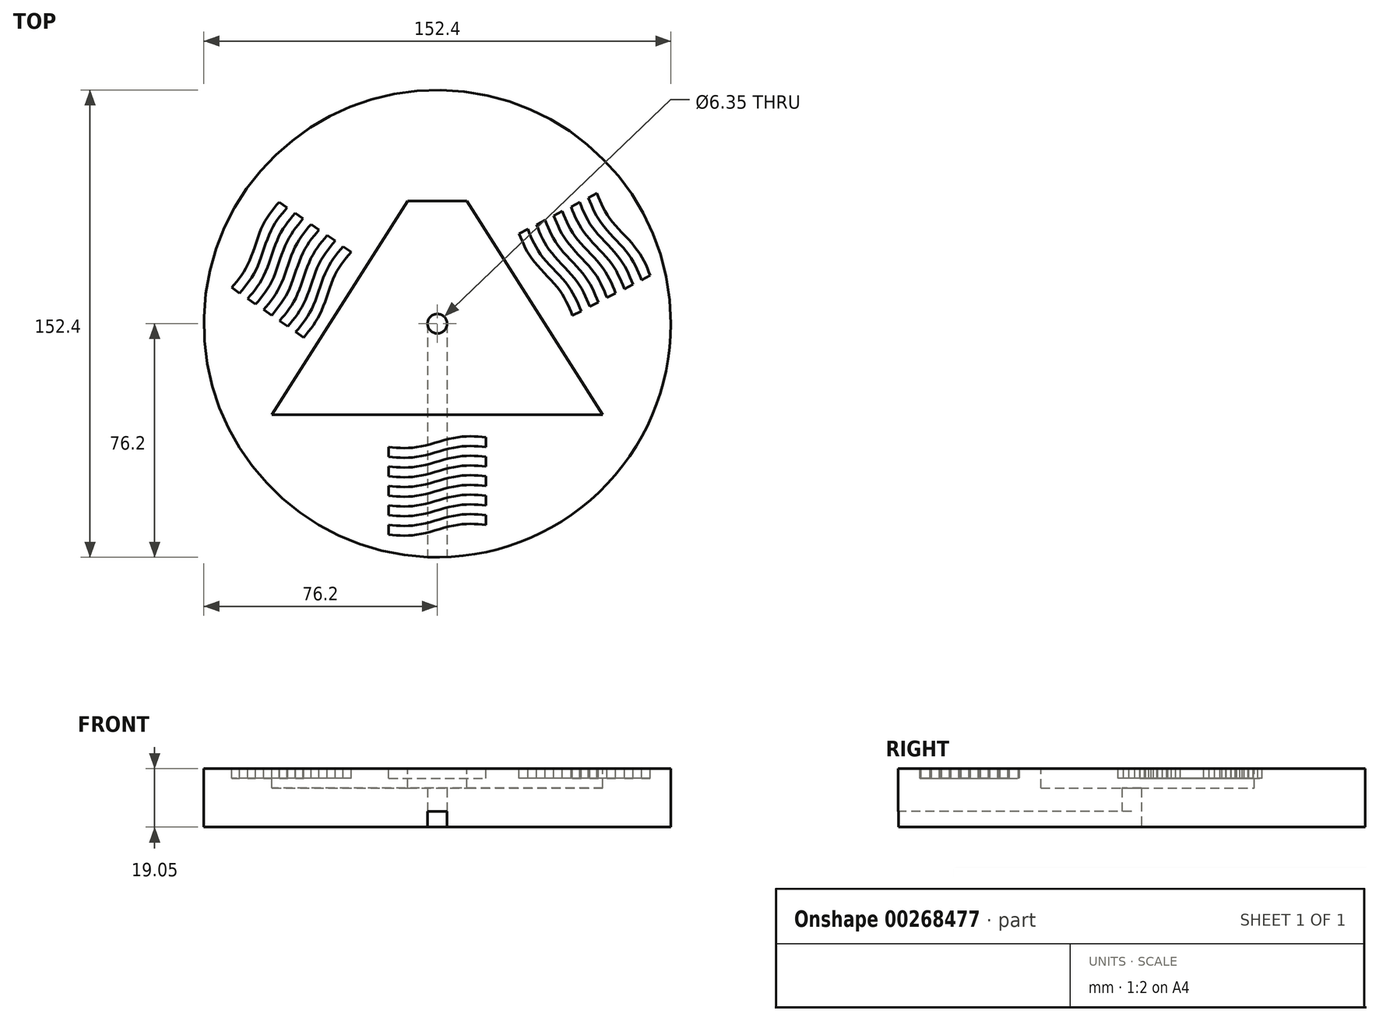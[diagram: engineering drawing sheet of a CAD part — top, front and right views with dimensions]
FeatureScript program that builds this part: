
annotation { "Feature Type Name" : "Feature", "Feature Type Description" : "" }
export const myFeature = defineFeature(function(context is Context, id is Id, definition is map)
    precondition{}
    {
        {
            var Q0;
            Q0=qCreatedBy(makeId("Top.planeOp"),FACE);
            var sketch = newSketch(context, id + "F0", { "sketchPlane" : qUnion([Q0])});
            skCircle(sketch, "E0", {"center": v(0, 0) * mm, "radius": 76.2 * mm});
            skCircle(sketch, "E1", {"center": v(0, 0) * mm, "radius": 3.18 * mm});
            skSolve(sketch);
        }
        {
            var Q0;
            Q0=qSketchRegion(id+"F0",true);
            extrude(context, id + "F1", {"entities" : qUnion([Q0]), "depth" : 19.05 * mm});
        }
        {
            var Q0;
            Q0=makeQuery(id+"F1.opExtrude","CAP_FACE",FACE,{"disambiguationData":[OSD([sQuery(id+"F0.wireOp",EDGE,"E0"),sQuery(id+"F0.wireOp",EDGE,"E1")])],"isStart":false});
            var sketch = newSketch(context, id + "F2", { "sketchPlane" : qUnion([Q0])});
            skLineSegment(sketch, "E2", {"start": v(-9.65, 39.97) * mm, "end": v(9.65, 39.97) * mm});
            skLineSegment(sketch, "E3", {"start": v(9.65, 39.97) * mm, "end": v(53.98, -29.68) * mm});
            skLineSegment(sketch, "E4", {"start": v(53.98, -29.68) * mm, "end": v(-53.97, -29.68) * mm});
            skLineSegment(sketch, "E5", {"start": v(-53.97, -29.68) * mm, "end": v(-9.65, 39.97) * mm});
            skSolve(sketch);
        }
        {
            var Q0;
            Q0=qSketchRegion(id+"F2",true);
            extrude(context, id + "F3", {"entities" : qUnion([Q0]), "operationType" : NewBodyOperationType.REMOVE, "oppositeDirection" : true, "depth" : 6.35 * mm});
        }
        {
            var Q0;
            Q0=makeQuery(id+"F1.opExtrude","CAP_FACE",FACE,{"disambiguationData":[OSD([sQuery(id+"F0.wireOp",EDGE,"E0"),sQuery(id+"F0.wireOp",EDGE,"E1")])],"isStart":false});
            var sketch = newSketch(context, id + "F4", { "sketchPlane" : qUnion([Q0])});
            skFitSpline(sketch, "E6", {"points": [v(-15.87, -68.82) * mm, v(-6.35, -68.82) * mm, v(6.35, -65.64) * mm, v(15.88, -65.64) * mm], "startDerivative": vector(28.9, -2.7) * mm, "endDerivative": vector(28.9, -2.7) * mm});
            skFitSpline(sketch, "E7", {"points": [v(-15.87, -65.64) * mm, v(-6.35, -65.64) * mm, v(6.35, -62.47) * mm, v(15.88, -62.47) * mm], "startDerivative": vector(28.9, -2.7) * mm, "endDerivative": vector(28.9, -2.7) * mm});
            skFitSpline(sketch, "E8", {"points": [v(-15.87, -62.47) * mm, v(-6.35, -62.47) * mm, v(6.35, -59.3) * mm, v(15.88, -59.3) * mm], "startDerivative": vector(28.9, -2.7) * mm, "endDerivative": vector(28.9, -2.7) * mm});
            skFitSpline(sketch, "E9", {"points": [v(-15.87, -59.3) * mm, v(-6.35, -59.3) * mm, v(6.35, -56.12) * mm, v(15.88, -56.12) * mm], "startDerivative": vector(28.9, -2.7) * mm, "endDerivative": vector(28.9, -2.7) * mm});
            skFitSpline(sketch, "E10", {"points": [v(-15.87, -56.12) * mm, v(-6.35, -56.12) * mm, v(6.35, -52.94) * mm, v(15.87, -52.94) * mm], "startDerivative": vector(28.9, -2.7) * mm, "endDerivative": vector(28.9, -2.7) * mm});
            skFitSpline(sketch, "E11", {"points": [v(-15.87, -52.94) * mm, v(-6.35, -52.94) * mm, v(6.35, -49.77) * mm, v(15.87, -49.77) * mm], "startDerivative": vector(28.9, -2.7) * mm, "endDerivative": vector(28.9, -2.7) * mm});
            skFitSpline(sketch, "E12", {"points": [v(-15.88, -49.77) * mm, v(-6.35, -49.77) * mm, v(6.35, -46.6) * mm, v(15.87, -46.6) * mm], "startDerivative": vector(28.9, -2.7) * mm, "endDerivative": vector(28.9, -2.7) * mm});
            skFitSpline(sketch, "E13", {"points": [v(-15.88, -46.6) * mm, v(-6.35, -46.6) * mm, v(6.35, -43.42) * mm, v(15.87, -43.42) * mm], "startDerivative": vector(28.9, -2.7) * mm, "endDerivative": vector(28.9, -2.7) * mm});
            skFitSpline(sketch, "E14", {"points": [v(-15.88, -43.42) * mm, v(-6.35, -43.42) * mm, v(6.35, -40.24) * mm, v(15.87, -40.24) * mm], "startDerivative": vector(28.9, -2.7) * mm, "endDerivative": vector(28.9, -2.7) * mm});
            skFitSpline(sketch, "E15", {"points": [v(-15.88, -40.24) * mm, v(-6.35, -40.24) * mm, v(6.35, -37.07) * mm, v(15.88, -37.07) * mm], "startDerivative": vector(28.9, -2.7) * mm, "endDerivative": vector(28.9, -2.7) * mm});
            skLineSegment(sketch, "E16", {"start": v(-15.88, -40.24) * mm, "end": v(-15.88, -43.42) * mm});
            skLineSegment(sketch, "E17", {"start": v(-15.88, -46.6) * mm, "end": v(-15.88, -49.77) * mm});
            skLineSegment(sketch, "E18", {"start": v(-15.87, -52.94) * mm, "end": v(-15.87, -56.12) * mm});
            skLineSegment(sketch, "E19", {"start": v(-15.87, -59.3) * mm, "end": v(-15.87, -62.47) * mm});
            skLineSegment(sketch, "E20", {"start": v(-15.87, -65.64) * mm, "end": v(-15.87, -68.82) * mm});
            skLineSegment(sketch, "E21", {"start": v(15.88, -65.64) * mm, "end": v(15.88, -62.47) * mm});
            skLineSegment(sketch, "E22", {"start": v(15.88, -59.3) * mm, "end": v(15.88, -56.12) * mm});
            skLineSegment(sketch, "E23", {"start": v(15.87, -52.94) * mm, "end": v(15.87, -49.77) * mm});
            skLineSegment(sketch, "E24", {"start": v(15.87, -46.6) * mm, "end": v(15.87, -43.42) * mm});
            skLineSegment(sketch, "E25", {"start": v(15.87, -40.24) * mm, "end": v(15.88, -37.07) * mm});
            skFitSpline(sketch, "E26", {"points": [v(69.46, 15.75) * mm, v(65.09, 24.2) * mm, v(56.44, 34.03) * mm, v(52.07, 42.5) * mm], "startDerivative": vector(-10.87, 26.93) * mm, "endDerivative": vector(-10.87, 26.93) * mm});
            skFitSpline(sketch, "E27", {"points": [v(66.64, 14.29) * mm, v(62.27, 22.75) * mm, v(53.62, 32.58) * mm, v(49.25, 41.04) * mm], "startDerivative": vector(-10.87, 26.93) * mm, "endDerivative": vector(-10.87, 26.93) * mm});
            skFitSpline(sketch, "E28", {"points": [v(63.82, 12.83) * mm, v(59.45, 21.3) * mm, v(50.8, 31.12) * mm, v(46.42, 39.58) * mm], "startDerivative": vector(-10.87, 26.93) * mm, "endDerivative": vector(-10.87, 26.93) * mm});
            skFitSpline(sketch, "E29", {"points": [v(61, 11.37) * mm, v(56.63, 19.84) * mm, v(47.98, 29.66) * mm, v(43.6, 38.12) * mm], "startDerivative": vector(-10.87, 26.93) * mm, "endDerivative": vector(-10.87, 26.93) * mm});
            skFitSpline(sketch, "E30", {"points": [v(58.18, 9.92) * mm, v(53.8, 18.38) * mm, v(45.16, 28.2) * mm, v(40.78, 36.66) * mm], "startDerivative": vector(-10.87, 26.93) * mm, "endDerivative": vector(-10.87, 26.93) * mm});
            skFitSpline(sketch, "E31", {"points": [v(55.36, 8.46) * mm, v(50.99, 16.92) * mm, v(42.34, 26.75) * mm, v(37.96, 35.2) * mm], "startDerivative": vector(-10.87, 26.93) * mm, "endDerivative": vector(-10.87, 26.93) * mm});
            skFitSpline(sketch, "E32", {"points": [v(52.54, 7) * mm, v(48.17, 15.46) * mm, v(39.51, 25.29) * mm, v(35.14, 33.75) * mm], "startDerivative": vector(-10.87, 26.93) * mm, "endDerivative": vector(-10.87, 26.93) * mm});
            skFitSpline(sketch, "E33", {"points": [v(49.72, 5.54) * mm, v(45.35, 14) * mm, v(36.7, 23.83) * mm, v(32.32, 32.3) * mm], "startDerivative": vector(-10.87, 26.93) * mm, "endDerivative": vector(-10.87, 26.93) * mm});
            skFitSpline(sketch, "E34", {"points": [v(46.9, 4.09) * mm, v(42.52, 12.55) * mm, v(33.87, 22.37) * mm, v(29.5, 30.83) * mm], "startDerivative": vector(-10.87, 26.93) * mm, "endDerivative": vector(-10.87, 26.93) * mm});
            skFitSpline(sketch, "E35", {"points": [v(44.08, 2.63) * mm, v(39.7, 11.1) * mm, v(31.05, 20.92) * mm, v(26.68, 29.38) * mm], "startDerivative": vector(-10.87, 26.93) * mm, "endDerivative": vector(-10.87, 26.93) * mm});
            skLineSegment(sketch, "E36", {"start": v(44.08, 2.63) * mm, "end": v(46.9, 4.09) * mm});
            skLineSegment(sketch, "E37", {"start": v(49.72, 5.54) * mm, "end": v(52.54, 7) * mm});
            skLineSegment(sketch, "E38", {"start": v(55.36, 8.46) * mm, "end": v(58.18, 9.92) * mm});
            skLineSegment(sketch, "E39", {"start": v(61, 11.37) * mm, "end": v(63.82, 12.83) * mm});
            skLineSegment(sketch, "E40", {"start": v(66.64, 14.29) * mm, "end": v(69.46, 15.75) * mm});
            skLineSegment(sketch, "E41", {"start": v(52.07, 42.5) * mm, "end": v(49.25, 41.04) * mm});
            skLineSegment(sketch, "E42", {"start": v(46.42, 39.58) * mm, "end": v(43.6, 38.12) * mm});
            skLineSegment(sketch, "E43", {"start": v(40.78, 36.66) * mm, "end": v(37.96, 35.2) * mm});
            skLineSegment(sketch, "E44", {"start": v(35.14, 33.75) * mm, "end": v(32.32, 32.3) * mm});
            skLineSegment(sketch, "E45", {"start": v(29.5, 30.83) * mm, "end": v(26.68, 29.38) * mm});
            skFitSpline(sketch, "E46", {"points": [v(-51.63, 39.67) * mm, v(-57.06, 31.84) * mm, v(-61.69, 19.6) * mm, v(-67.12, 11.77) * mm], "startDerivative": vector(-18.7, -22.21) * mm, "endDerivative": vector(-18.7, -22.21) * mm});
            skFitSpline(sketch, "E47", {"points": [v(-49.02, 37.86) * mm, v(-54.45, 30.03) * mm, v(-59.08, 17.78) * mm, v(-64.5, 9.96) * mm], "startDerivative": vector(-18.7, -22.21) * mm, "endDerivative": vector(-18.7, -22.21) * mm});
            skFitSpline(sketch, "E48", {"points": [v(-46.41, 36.05) * mm, v(-51.84, 28.22) * mm, v(-56.47, 15.98) * mm, v(-61.9, 8.15) * mm], "startDerivative": vector(-18.7, -22.21) * mm, "endDerivative": vector(-18.7, -22.21) * mm});
            skFitSpline(sketch, "E49", {"points": [v(-43.8, 34.24) * mm, v(-49.23, 26.41) * mm, v(-53.86, 14.17) * mm, v(-59.3, 6.34) * mm], "startDerivative": vector(-18.7, -22.21) * mm, "endDerivative": vector(-18.7, -22.21) * mm});
            skFitSpline(sketch, "E50", {"points": [v(-41.2, 32.43) * mm, v(-46.63, 24.6) * mm, v(-51.25, 12.36) * mm, v(-56.68, 4.53) * mm], "startDerivative": vector(-18.7, -22.21) * mm, "endDerivative": vector(-18.7, -22.21) * mm});
            skFitSpline(sketch, "E51", {"points": [v(-38.59, 30.62) * mm, v(-44.02, 22.8) * mm, v(-48.64, 10.55) * mm, v(-54.07, 2.72) * mm], "startDerivative": vector(-18.7, -22.21) * mm, "endDerivative": vector(-18.7, -22.21) * mm});
            skFitSpline(sketch, "E52", {"points": [v(-35.98, 28.8) * mm, v(-41.4, 20.98) * mm, v(-46.04, 8.74) * mm, v(-51.46, 0.91) * mm], "startDerivative": vector(-18.7, -22.21) * mm, "endDerivative": vector(-18.7, -22.21) * mm});
            skFitSpline(sketch, "E53", {"points": [v(-33.37, 27) * mm, v(-38.8, 19.17) * mm, v(-43.43, 6.93) * mm, v(-48.86, -0.9) * mm], "startDerivative": vector(-18.7, -22.21) * mm, "endDerivative": vector(-18.7, -22.21) * mm});
            skFitSpline(sketch, "E54", {"points": [v(-30.76, 25.2) * mm, v(-36.19, 17.36) * mm, v(-40.82, 5.12) * mm, v(-46.25, -2.7) * mm], "startDerivative": vector(-18.7, -22.21) * mm, "endDerivative": vector(-18.7, -22.21) * mm});
            skFitSpline(sketch, "E55", {"points": [v(-28.15, 23.38) * mm, v(-33.58, 15.55) * mm, v(-38.2, 3.3) * mm, v(-43.64, -4.52) * mm], "startDerivative": vector(-18.7, -22.21) * mm, "endDerivative": vector(-18.7, -22.21) * mm});
            skLineSegment(sketch, "E56", {"start": v(-28.15, 23.38) * mm, "end": v(-30.76, 25.2) * mm});
            skLineSegment(sketch, "E57", {"start": v(-33.37, 27) * mm, "end": v(-35.98, 28.8) * mm});
            skLineSegment(sketch, "E58", {"start": v(-38.59, 30.62) * mm, "end": v(-41.2, 32.43) * mm});
            skLineSegment(sketch, "E59", {"start": v(-43.8, 34.24) * mm, "end": v(-46.41, 36.05) * mm});
            skLineSegment(sketch, "E60", {"start": v(-49.02, 37.86) * mm, "end": v(-51.63, 39.67) * mm});
            skLineSegment(sketch, "E61", {"start": v(-67.12, 11.77) * mm, "end": v(-64.5, 9.96) * mm});
            skLineSegment(sketch, "E62", {"start": v(-61.9, 8.15) * mm, "end": v(-59.3, 6.34) * mm});
            skLineSegment(sketch, "E63", {"start": v(-56.68, 4.53) * mm, "end": v(-54.07, 2.72) * mm});
            skLineSegment(sketch, "E64", {"start": v(-51.46, 0.91) * mm, "end": v(-48.86, -0.9) * mm});
            skLineSegment(sketch, "E65", {"start": v(-46.25, -2.7) * mm, "end": v(-43.64, -4.52) * mm});
            skSolve(sketch);
        }
        {
            var Q0;
            Q0=makeQuery(id+"F4.imprint","IMPRINT",FACE,{"disambiguationData":[TD([[makeQuery(id+"F4.imprint","IMPRINT",EDGE,{"derivedFrom":sQuery(id+"F4.wireOp",EDGE,"E6")}),1.0]])]});
            var Q1;
            Q1=makeQuery(id+"F4.imprint","IMPRINT",FACE,{"disambiguationData":[TD([[makeQuery(id+"F4.imprint","IMPRINT",EDGE,{"derivedFrom":sQuery(id+"F4.wireOp",EDGE,"E8")}),1.0]])]});
            var Q2;
            Q2=makeQuery(id+"F4.imprint","IMPRINT",FACE,{"disambiguationData":[TD([[makeQuery(id+"F4.imprint","IMPRINT",EDGE,{"derivedFrom":sQuery(id+"F4.wireOp",EDGE,"E10")}),1.0]])]});
            var Q3;
            Q3=makeQuery(id+"F4.imprint","IMPRINT",FACE,{"disambiguationData":[TD([[makeQuery(id+"F4.imprint","IMPRINT",EDGE,{"derivedFrom":sQuery(id+"F4.wireOp",EDGE,"E12")}),1.0]])]});
            var Q4;
            Q4=makeQuery(id+"F4.imprint","IMPRINT",FACE,{"disambiguationData":[TD([[makeQuery(id+"F4.imprint","IMPRINT",EDGE,{"derivedFrom":sQuery(id+"F4.wireOp",EDGE,"E14")}),1.0]])]});
            var Q5;
            Q5=makeQuery(id+"F4.imprint","IMPRINT",FACE,{"disambiguationData":[TD([[makeQuery(id+"F4.imprint","IMPRINT",EDGE,{"derivedFrom":sQuery(id+"F4.wireOp",EDGE,"E54")}),1.0]])]});
            var Q6;
            Q6=makeQuery(id+"F4.imprint","IMPRINT",FACE,{"disambiguationData":[TD([[makeQuery(id+"F4.imprint","IMPRINT",EDGE,{"derivedFrom":sQuery(id+"F4.wireOp",EDGE,"E52")}),1.0]])]});
            var Q7;
            Q7=makeQuery(id+"F4.imprint","IMPRINT",FACE,{"disambiguationData":[TD([[makeQuery(id+"F4.imprint","IMPRINT",EDGE,{"derivedFrom":sQuery(id+"F4.wireOp",EDGE,"E50")}),1.0]])]});
            var Q8;
            Q8=makeQuery(id+"F4.imprint","IMPRINT",FACE,{"disambiguationData":[TD([[makeQuery(id+"F4.imprint","IMPRINT",EDGE,{"derivedFrom":sQuery(id+"F4.wireOp",EDGE,"E48")}),1.0]])]});
            var Q9;
            Q9=makeQuery(id+"F4.imprint","IMPRINT",FACE,{"disambiguationData":[TD([[makeQuery(id+"F4.imprint","IMPRINT",EDGE,{"derivedFrom":sQuery(id+"F4.wireOp",EDGE,"E46")}),1.0]])]});
            var Q10;
            Q10=makeQuery(id+"F4.imprint","IMPRINT",FACE,{"disambiguationData":[TD([[makeQuery(id+"F4.imprint","IMPRINT",EDGE,{"derivedFrom":sQuery(id+"F4.wireOp",EDGE,"E34")}),1.0]])]});
            var Q11;
            Q11=makeQuery(id+"F4.imprint","IMPRINT",FACE,{"disambiguationData":[TD([[makeQuery(id+"F4.imprint","IMPRINT",EDGE,{"derivedFrom":sQuery(id+"F4.wireOp",EDGE,"E32")}),1.0]])]});
            var Q12;
            Q12=makeQuery(id+"F4.imprint","IMPRINT",FACE,{"disambiguationData":[TD([[makeQuery(id+"F4.imprint","IMPRINT",EDGE,{"derivedFrom":sQuery(id+"F4.wireOp",EDGE,"E30")}),1.0]])]});
            var Q13;
            Q13=makeQuery(id+"F4.imprint","IMPRINT",FACE,{"disambiguationData":[TD([[makeQuery(id+"F4.imprint","IMPRINT",EDGE,{"derivedFrom":sQuery(id+"F4.wireOp",EDGE,"E28")}),1.0]])]});
            var Q14;
            Q14=makeQuery(id+"F4.imprint","IMPRINT",FACE,{"disambiguationData":[TD([[makeQuery(id+"F4.imprint","IMPRINT",EDGE,{"derivedFrom":sQuery(id+"F4.wireOp",EDGE,"E26")}),1.0]])]});
            var Q15;
            Q15=sQuery(id+"F4.wireOp",EDGE,"E14");
            var Q16;
            Q16=sQuery(id+"F4.wireOp",EDGE,"E8");
            var Q17;
            Q17=sQuery(id+"F4.wireOp",EDGE,"E7");
            var Q18;
            Q18=sQuery(id+"F4.wireOp",EDGE,"E6");
            var Q19;
            Q19=sQuery(id+"F4.wireOp",EDGE,"E9");
            var Q20;
            Q20=sQuery(id+"F4.wireOp",EDGE,"E13");
            var Q21;
            Q21=sQuery(id+"F4.wireOp",EDGE,"E15");
            var Q22;
            Q22=sQuery(id+"F4.wireOp",EDGE,"E10");
            var Q23;
            Q23=sQuery(id+"F4.wireOp",EDGE,"E12");
            var Q24;
            Q24=sQuery(id+"F4.wireOp",EDGE,"E11");
            var Q25;
            Q25=sQuery(id+"F4.wireOp",EDGE,"E16");
            var Q26;
            Q26=sQuery(id+"F4.wireOp",EDGE,"E24");
            var Q27;
            Q27=sQuery(id+"F4.wireOp",EDGE,"E21");
            var Q28;
            Q28=sQuery(id+"F4.wireOp",EDGE,"E18");
            var Q29;
            Q29=sQuery(id+"F4.wireOp",EDGE,"E19");
            var Q30;
            Q30=sQuery(id+"F4.wireOp",EDGE,"E25");
            var Q31;
            Q31=sQuery(id+"F4.wireOp",EDGE,"E17");
            var Q32;
            Q32=sQuery(id+"F4.wireOp",EDGE,"E23");
            var Q33;
            Q33=sQuery(id+"F4.wireOp",EDGE,"E22");
            var Q34;
            Q34=sQuery(id+"F4.wireOp",EDGE,"E20");
            extrude(context, id + "F5", {"entities" : qUnion([Q0, Q1, Q2, Q3, Q4, Q5, Q6, Q7, Q8, Q9, Q10, Q11, Q12, Q13, Q14]), "operationType" : NewBodyOperationType.REMOVE, "surfaceEntities" : qUnion([Q15, Q16, Q17, Q18, Q19, Q20, Q21, Q22, Q23, Q24, Q25, Q26, Q27, Q28, Q29, Q30, Q31, Q32, Q33, Q34]), "oppositeDirection" : true, "depth" : 3.17 * mm});
        }
        {
            var Q0;
            Q0=makeQuery(id+"F1.opExtrude","CAP_FACE",FACE,{"disambiguationData":[OSD([sQuery(id+"F0.wireOp",EDGE,"E0"),sQuery(id+"F0.wireOp",EDGE,"E1")])],"isStart":true});
            var sketch = newSketch(context, id + "F6", { "sketchPlane" : qUnion([Q0])});
            skLineSegment(sketch, "E66.bottom", {"start": v(-3.18, 0) * mm, "end": v(3.17, 0) * mm});
            skLineSegment(sketch, "E66.top", {"start": v(-3.18, 80.54) * mm, "end": v(3.17, 80.54) * mm});
            skLineSegment(sketch, "E66.left", {"start": v(-3.18, 0) * mm, "end": v(-3.18, 80.54) * mm});
            skLineSegment(sketch, "E66.right", {"start": v(3.17, 0) * mm, "end": v(3.17, 80.54) * mm});
            skSolve(sketch);
        }
        {
            var Q0;
            Q0 = qSketchRegion(id + "F6", true);
            extrude(context, id + "F7", {"entities" : qUnion([Q0]), "operationType" : NewBodyOperationType.REMOVE, "oppositeDirection" : true, "depth" : 5.08 * mm});
        }
    });
